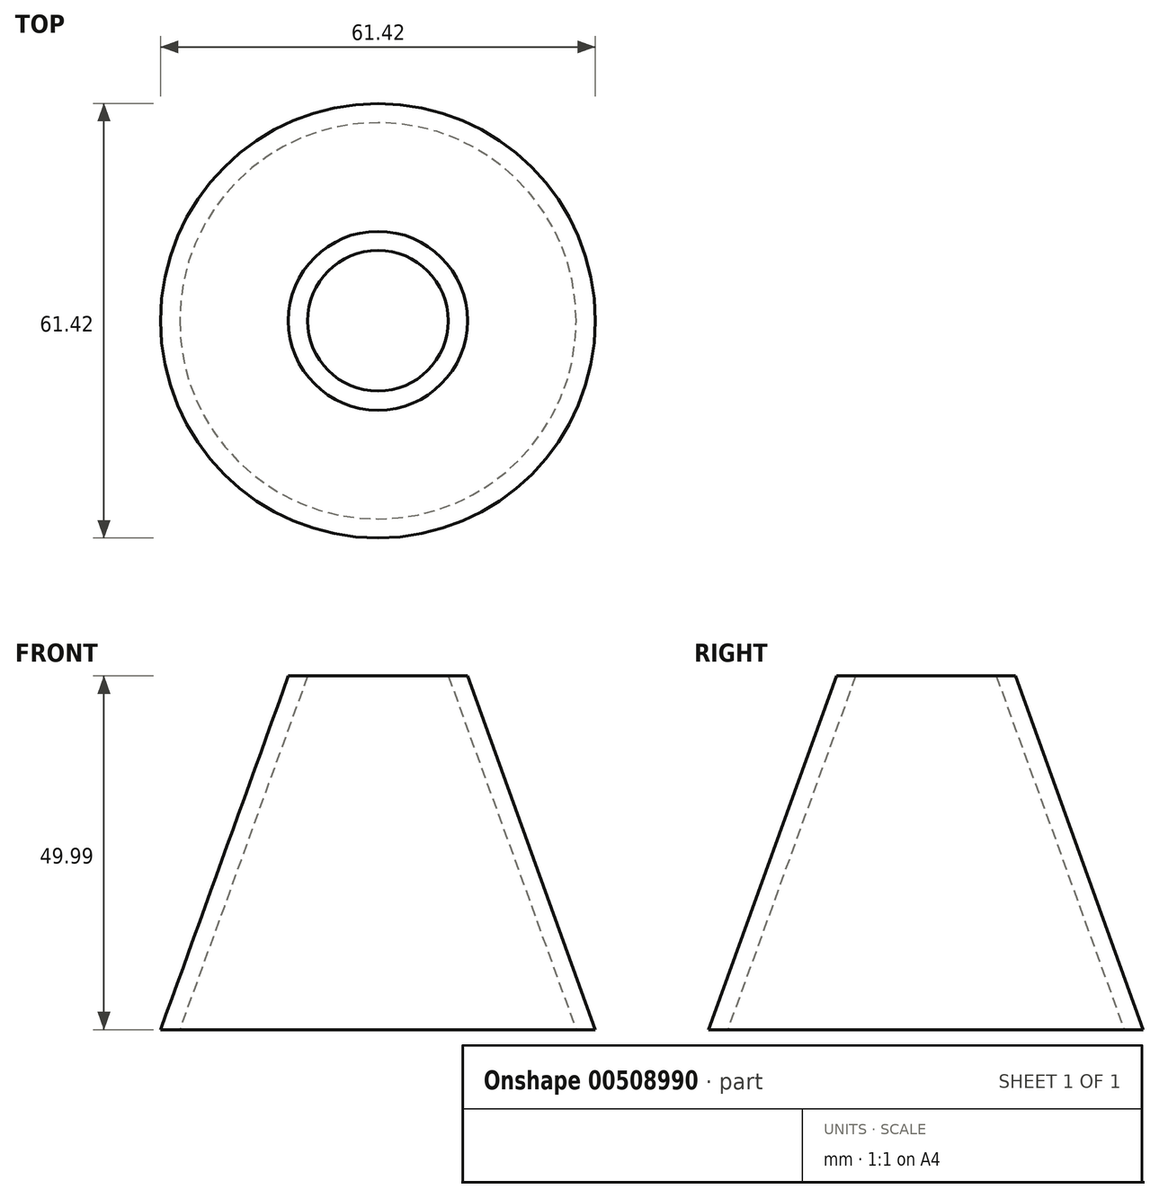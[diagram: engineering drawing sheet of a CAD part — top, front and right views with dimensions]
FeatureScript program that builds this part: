
annotation { "Feature Type Name" : "Feature", "Feature Type Description" : "" }
export const myFeature = defineFeature(function(context is Context, id is Id, definition is map)
    precondition{}
    {
        {
            var Q0;
            Q0=qCreatedBy(makeId("Front.planeOp"),FACE);
            var sketch = newSketch(context, id + "F0", { "sketchPlane" : qUnion([Q0])});
            skLineSegment(sketch, "E0", {"start": v(0, 49.99) * mm, "end": v(12.65, 49.99) * mm});
            skLineSegment(sketch, "E1", {"start": v(12.65, 49.99) * mm, "end": v(30.7, 0) * mm});
            skLineSegment(sketch, "E2", {"start": v(30.7, 0) * mm, "end": v(0, 0) * mm});
            skLineSegment(sketch, "E3", {"start": v(0, 0) * mm, "end": v(0, 49.99) * mm});
            skPoint(sketch, "E4", {"position": v(21.68, 25) * mm});
            skSolve(sketch);
        }
        {
            var Q0;
            Q0=makeQuery(id+"F0.imprint","IMPRINT",FACE,{"disambiguationData":[TD([[makeQuery(id+"F0.imprint","IMPRINT",EDGE,{"derivedFrom":sQuery(id+"F0.wireOp",EDGE,"E0")}),-1.0]])]});
            var Q1;
            Q1=sQuery(id+"F0.wireOp",EDGE,"E3");
            revolve(context, id + "F1", {"entities" : qUnion([Q0]), "axis" : qUnion([Q1]), "revolveType" : RevolveType.FULL});
        }
        {
            var Q0;
            Q0=makeQuery(id+"F1.opRevolve","SWEPT_FACE",FACE,{"disambiguationData":[OSD([sQuery(id+"F0.wireOp",EDGE,"E2")])]});
            var Q1;
            Q1=makeQuery(id+"F1.opRevolve","SWEPT_FACE",FACE,{"disambiguationData":[OSD([sQuery(id+"F0.wireOp",EDGE,"E0")])]});
            shell(context, id + "F2", {"entities" : qUnion([Q0, Q1]), "thickness" : 2.54 * mm});
        }
    });
